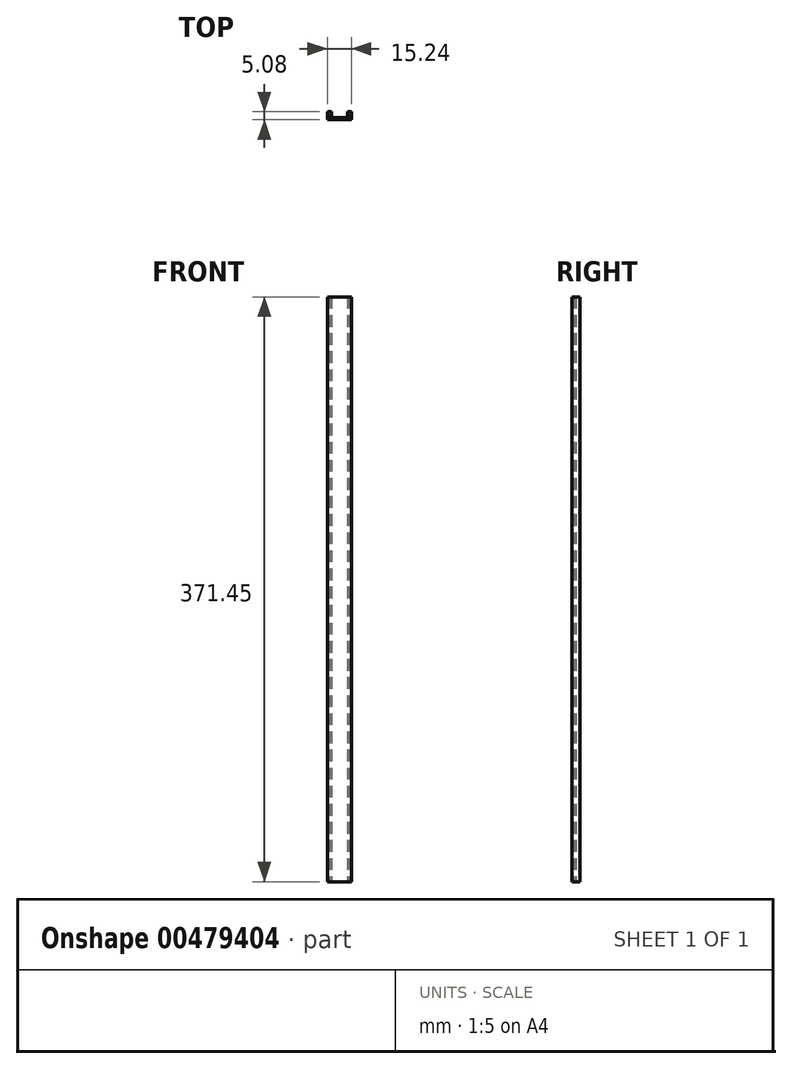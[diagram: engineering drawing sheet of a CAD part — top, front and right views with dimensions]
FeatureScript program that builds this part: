
annotation { "Feature Type Name" : "Feature", "Feature Type Description" : "" }
export const myFeature = defineFeature(function(context is Context, id is Id, definition is map)
    precondition{}
    {
        {
            var Q0;
            Q0=qCreatedBy(makeId("Top.planeOp"),FACE);
            var sketch = newSketch(context, id + "F0", { "sketchPlane" : qUnion([Q0])});
            skLineSegment(sketch, "E0.bottom", {"start": v(0, 0) * mm, "end": v(7.62, 0) * mm});
            skLineSegment(sketch, "E0.top", {"start": v(0, 5.08) * mm, "end": v(7.62, 5.08) * mm});
            skLineSegment(sketch, "E0.left", {"start": v(0, 0) * mm, "end": v(0, 5.08) * mm});
            skLineSegment(sketch, "E0.right", {"start": v(7.62, 0) * mm, "end": v(7.62, 5.08) * mm});
            skLineSegment(sketch, "E1", {"start": v(2.54, 5.08) * mm, "end": v(2.54, 2.54) * mm});
            skLineSegment(sketch, "E2", {"start": v(2.54, 2.54) * mm, "end": v(1.27, 2.54) * mm});
            skLineSegment(sketch, "E3", {"start": v(1.27, 2.54) * mm, "end": v(1.27, 1.27) * mm});
            skLineSegment(sketch, "E4", {"start": v(1.27, 1.27) * mm, "end": v(7.62, 1.27) * mm});
            skSolve(sketch);
        }
        {
            var Q0;
            {var subQ1=sQuery(id+"F0.wireOp",EDGE,"E0.bottom");Q0=makeQuery(id+"F0.imprint","IMPRINT",FACE,{"disambiguationData":[TD([[makeQuery(id+"F0.imprint","IMPRINT",EDGE,{"derivedFrom":subQ1}),1.0]])]});}
            extrude(context, id + "F1", {"entities" : qUnion([Q0]), "depth" : 371.45 * mm, "offsetDistance" : 25.4 * mm});
        }
        {
            var Q0;
            Q0=makeQuery(id+"F1.opExtrude","SWEPT_BODY",BODY,{"disambiguationData":[OSD([sQuery(id+"F0.wireOp",EDGE,"E0.bottom"),sQuery(id+"F0.wireOp",EDGE,"E0.top"),sQuery(id+"F0.wireOp",EDGE,"E0.left"),sQuery(id+"F0.wireOp",EDGE,"E0.right"),sQuery(id+"F0.wireOp",EDGE,"E1"),sQuery(id+"F0.wireOp",EDGE,"E2"),sQuery(id+"F0.wireOp",EDGE,"E3"),sQuery(id+"F0.wireOp",EDGE,"E4")])]});
            var Q1;
            Q1=makeQuery(id+"F1.opExtrude","SWEPT_FACE",FACE,{"disambiguationData":[OSD([sQuery(id+"F0.wireOp",EDGE,"E0.right")])]});
            mirror(context, id + "F2", {"operationType" : NewBodyOperationType.ADD, "entities" : qUnion([Q0]), "mirrorPlane" : qUnion([Q1])});
        }
    });
